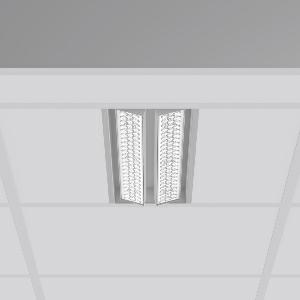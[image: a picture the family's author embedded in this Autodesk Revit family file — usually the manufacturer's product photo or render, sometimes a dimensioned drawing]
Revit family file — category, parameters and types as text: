
# Revit family: tx-move_901738_004_2_76_d4e3
name_source: partatom
category: Lighting Fixtures
units: mm (PartAtom-declared; Revit-internal decimal feet)

## family parameters
Cut with Voids When Loaded = No
Host = Face
Light Source = No
Part Type = Normal
Room Calculation Point = No
Round Connector Dimension = Use Diameter
Shared = No

## types (1)
- MultiLumen 1 (1 x LED Modul 927, 1925 lm, 2700)
    Apparent Load = 32 VA
    Approval mark = CE
    CIE Flux Codes = 65 90 98 100 100
    Color Rendering = 92
    Color Temperature = 2700
    Default Elevation = 1800 mm
    Description = Series: TX-MOVE
Einlege/Einbau-Flächenstrahler. Housing: sheet steel, powder-coated. 2xSwivel range: 90°. High-efficiency LED units with optimum light control thanks to clear plastic (PC) lens optics. Spezielle Mikrostrukturen reduzieren Gelbsaum. Asymmetrical light distribution. Suitable for laying in grid ceiling module 625. Connected converter included in separate gearbox.Suitable for through-wiring.MultiLumen: Luminous flux adjustable in 3 steps. Accessories: Mounting frame for installation in suspended ceilings. Environmentally friendly and resource-saving due to replaceable and recyclable components. 
Colour: silver, matt (approx. RAL 9006)
Length: 622 mm
Width: 190 mm
Height: 39 mm
Cut-out length: 602 mm
Cut-out width: 174 mm
Recess height: 100 mm
Lamp: LED
Socket: without socket
Colour temperature: 2700K
Colour rendering index (CRI): 90
System power: 32 W
Rated luminous flux: 3850 lm
Luminous efficiency: 120 lm/W
System power 2: 43 W
Rated luminous flux 2: 4850 lm
Luminous efficiency 2: 113 lm/W
System power 3: 62 W
Rated luminous flux 3: 6450 lm
Luminous efficiency 3: 104 lm/W
Control gear: Dimmable EVG, DALI
Protection class: I
Type of protection: IP 20
    Height = 0 mm  [stored 0 ft]
    Lamp = 1 x LED Modul 927
    Lamp Light Flux = 1925 lm
    Lamp count = 1
    Length = 622 mm
    Lifetime = 50000 h
    Luminous efficacy = 120 lm/W
    Manufacturer = RZB
    ModVariant = No
    Model = 901738.004.2.76
    Mounting Place = Ceiling, Wall
    Mounting Type = Recessed
    Number of Poles = 1
    OnlyDefault = Yes
    Power Factor = 1
    Product Name = TX-MOVE
    Product group = Recessed projectors
    ProductGroupID = 401
    Protection Class = Protection class I
    Protection Degree = IP 20
    RLX_Detail_Level = 1
    RLX_Emergency_Light_Flux = 0 lm
    RLX_Emergency_Type = 0
    RLX_Emergency_Type_DB = No
    RlxData = <blob elided: 55281 chars, md5=2b209a1a>
    Socket = socket
    Standby Power = 0 W
    System Light Flux = 3850 lm
    System Power = 32 W
    Type Comments = MultiLumen 1
    Type Image = 901737.004.jpg
    URL = http://relux.com
    VarID = multilumen_1
    Voltage = 230 V
    Voltage Range = 220-240 V
    Weight = 0.00 kg
    Width = 190 mm

note: [stored X ft] marks values corroborated as IEEE doubles in the binary element streams (Revit-internal decimal feet)

## geometry (parser evidence)
native form markers: Blend x4, Sweep x17
no freeform markers — native parametric forms only
